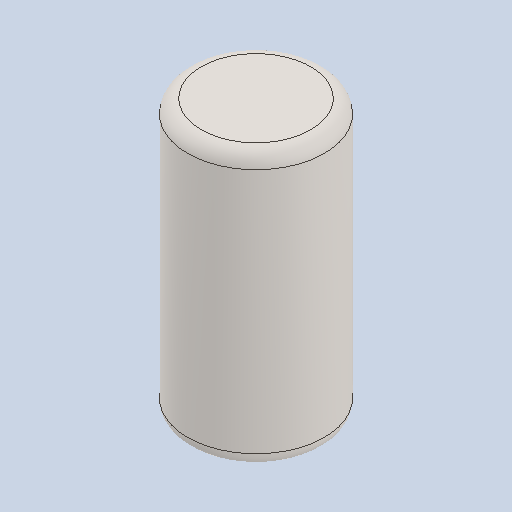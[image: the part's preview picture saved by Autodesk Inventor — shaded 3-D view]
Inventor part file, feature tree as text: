
AUTODESK INVENTOR PART (.ipt)
format: ipt  version: 2024.2 (Build 282272000, 272)  size: 102,912 bytes
history: native  units: in
note: dims shown in document units (in); Inventor stores cm internally (conversion verified against a paired STEP export)
features: fillet x1
ambient origin geometry x8: Origin, YZ Plane, XZ Plane, XY Plane, X Axis, Y Axis, Z Axis, Center Point
bodies: Solid1 (feature_tree)
feature tree (1):
  fillet  "Fillet1"  [1 undecoded]
note: 1 required parameter value undecoded (feature->parameter linkage not recoverable at this tier; creation-order binding heuristic only, values carry confidence <= 0.55)
